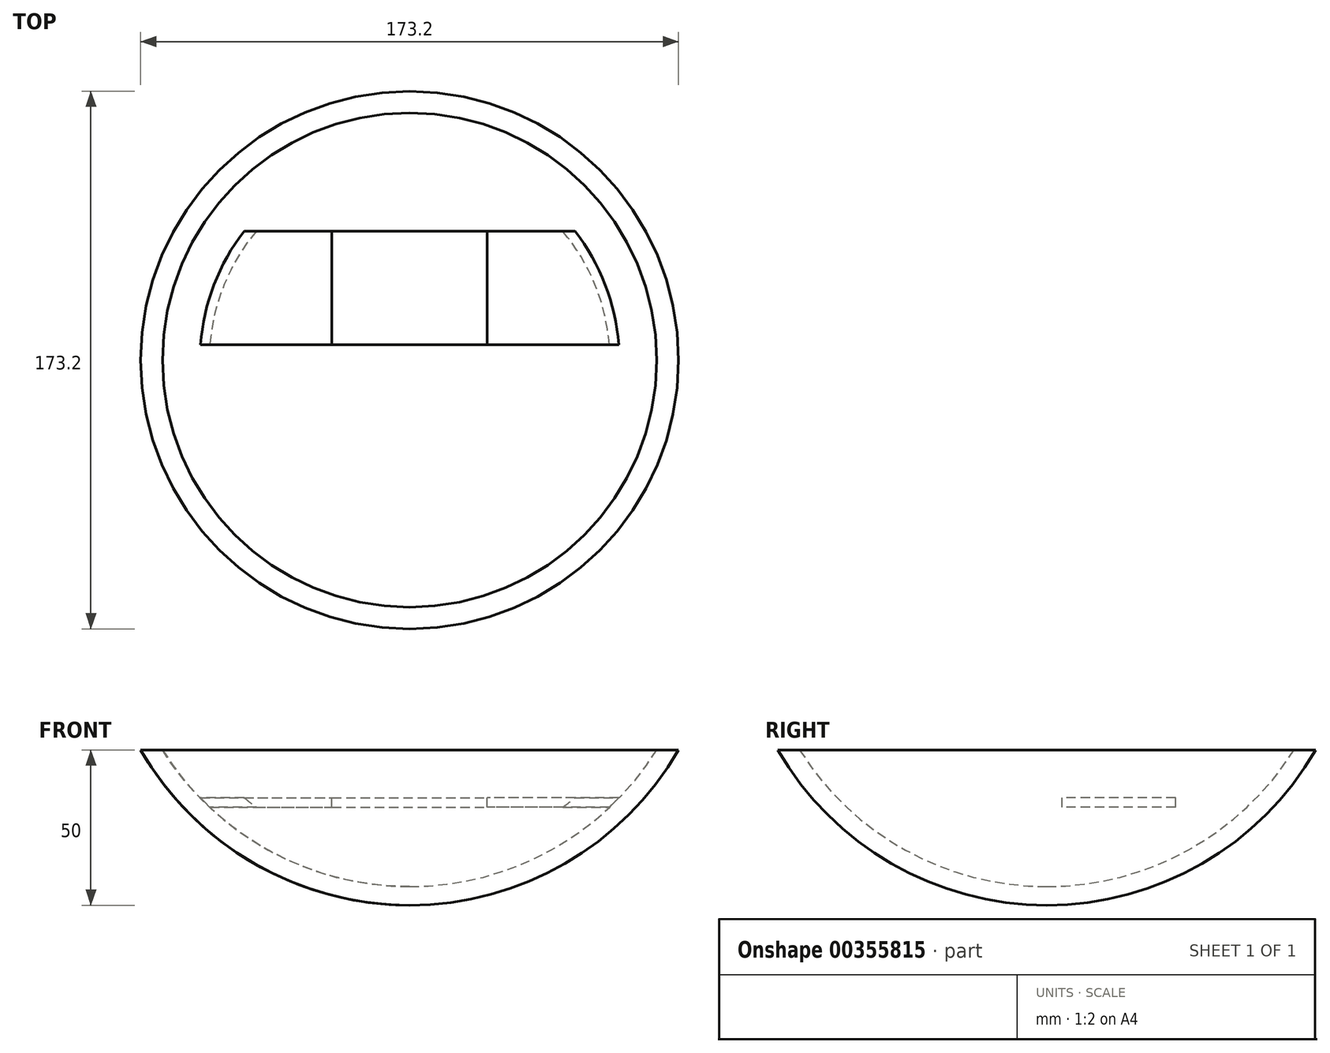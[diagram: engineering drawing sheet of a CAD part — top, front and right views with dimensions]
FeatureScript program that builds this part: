
annotation { "Feature Type Name" : "Feature", "Feature Type Description" : "" }
export const myFeature = defineFeature(function(context is Context, id is Id, definition is map)
    precondition{}
    {
        {
            var Q0;
            Q0=qCreatedBy(makeId("Front.planeOp"),FACE);
            var sketch = newSketch(context, id + "F0", { "sketchPlane" : qUnion([Q0])});
            skArc(sketch, "E0", {"start": v(-86.6, -50) * mm, "mid": v(-50, -86.6) * mm, "end": v(0, -100) * mm});
            skLineSegment(sketch, "E1", {"start": v(0, -50) * mm, "end": v(0, -100) * mm});
            skLineSegment(sketch, "E2", {"start": v(0, -50) * mm, "end": v(-86.6, -50) * mm});
            skPoint(sketch, "E3.orphan", {"position": v(0, 100) * mm});
            skSolve(sketch);
        }
        {
            var Q0;
            Q0=makeQuery(id+"F0.imprint","IMPRINT",FACE,{"disambiguationData":[TD([[makeQuery(id+"F0.imprint","IMPRINT",EDGE,{"derivedFrom":sQuery(id+"F0.wireOp",EDGE,"E0")}),1.0]])]});
            var Q1;
            Q1=sQuery(id+"F0.wireOp",EDGE,"E1");
            revolve(context, id + "F1", {"entities" : qUnion([Q0]), "axis" : qUnion([Q1]), "revolveType" : RevolveType.FULL});
        }
        {
            var Q0;
            Q0=makeQuery(id+"F1.opRevolve","SWEPT_FACE",FACE,{"disambiguationData":[OSD([sQuery(id+"F0.wireOp",EDGE,"E2")])]});
            shell(context, id + "F2", {"entities" : qUnion([Q0]), "thickness" : 6 * mm});
        }
        {
            var Q0;
            Q0=qCreatedBy(makeId("Front.planeOp"),FACE);
            cPlane(context, id + "F3", {"entities" : qUnion([Q0]), "cplaneType" : CPlaneType.OFFSET, "offset" : 5 * mm, "oppositeDirection" : true, "width" : 150 * mm, "height" : 150 * mm});
        }
        {
            var Q0;
            Q0=qCreatedBy(id+"F3.planeOp",FACE);
            var sketch = newSketch(context, id + "F4", { "sketchPlane" : qUnion([Q0])});
            skLineSegment(sketch, "E4.bottom", {"start": v(-25, -68.4) * mm, "end": v(25, -68.4) * mm});
            skLineSegment(sketch, "E4.top", {"start": v(-25, -65.4) * mm, "end": v(25, -65.4) * mm});
            skLineSegment(sketch, "E4.left", {"start": v(-25, -68.4) * mm, "end": v(-25, -65.4) * mm});
            skLineSegment(sketch, "E4.right", {"start": v(25, -68.4) * mm, "end": v(25, -65.4) * mm});
            skSolve(sketch);
        }
        {
            var Q0;
            Q0=qSketchRegion(id+"F4",true);
            extrude(context, id + "F5", {"entities" : qUnion([Q0]), "oppositeDirection" : true, "depth" : 36.5 * mm});
        }
        {
            var Q0;
            Q0=makeQuery(id+"F5.opExtrude","SWEPT_FACE",FACE,{"disambiguationData":[OSD([sQuery(id+"F4.wireOp",EDGE,"E4.right")])]});
            extrude(context, id + "F6", {"entities" : qUnion([Q0]), "endBound" : BoundingType.UP_TO_NEXT, "depth" : 25 * mm});
        }
        {
            var Q0;
            Q0=makeQuery(id+"F5.opExtrude","SWEPT_FACE",FACE,{"disambiguationData":[OSD([sQuery(id+"F4.wireOp",EDGE,"E4.left")])]});
            extrude(context, id + "F7", {"entities" : qUnion([Q0]), "endBound" : BoundingType.UP_TO_NEXT, "depth" : 25 * mm});
        }
    });
